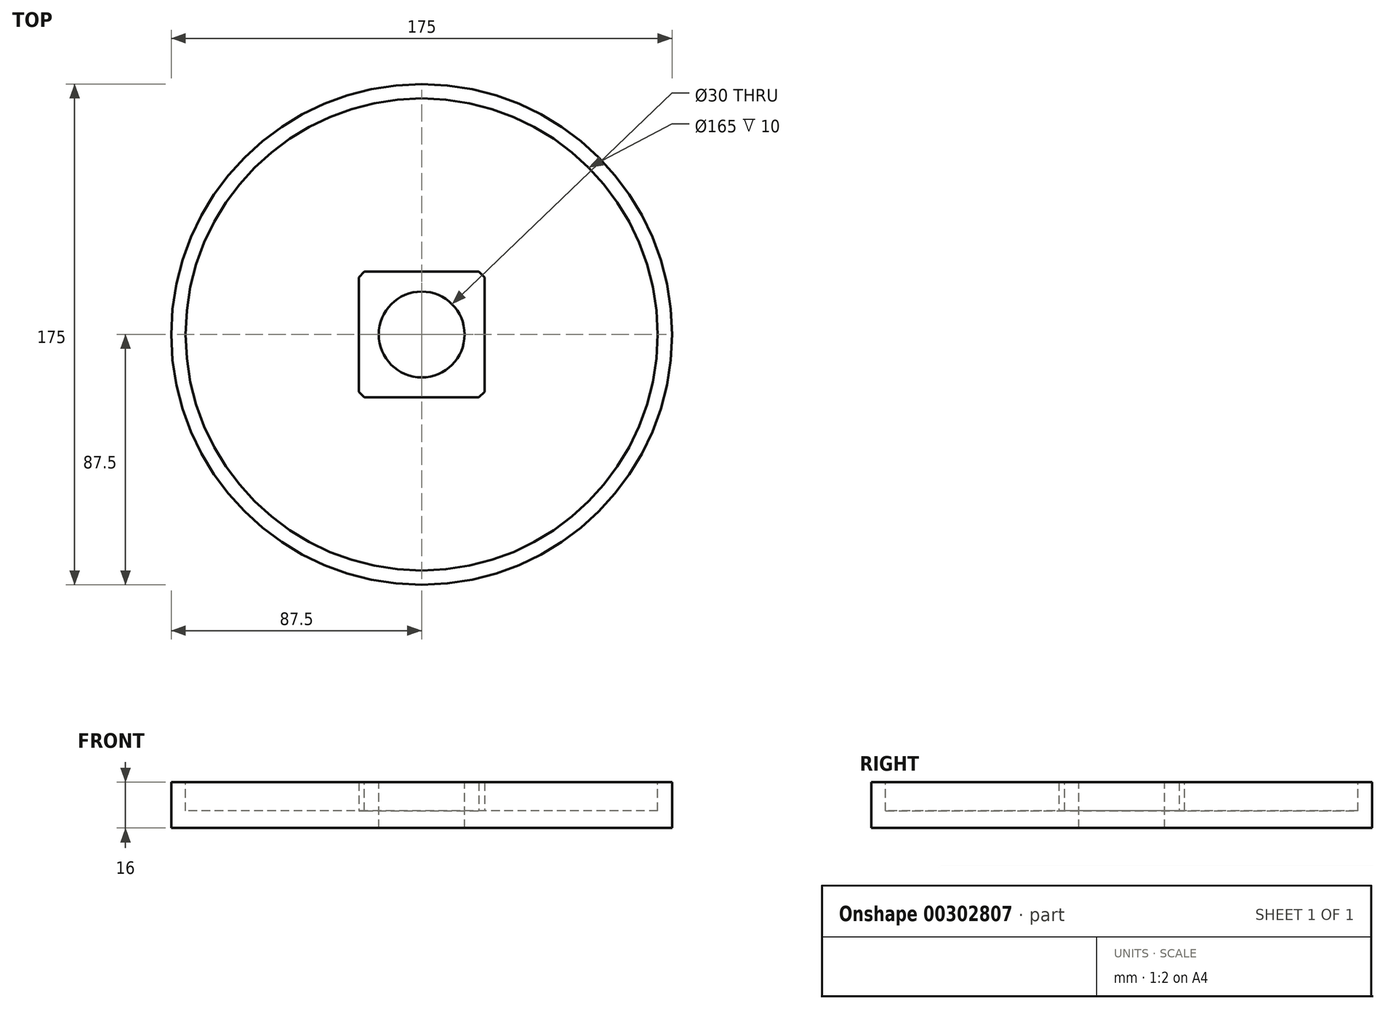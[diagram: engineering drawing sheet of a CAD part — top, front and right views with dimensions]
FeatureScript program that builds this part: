
annotation { "Feature Type Name" : "Feature", "Feature Type Description" : "" }
export const myFeature = defineFeature(function(context is Context, id is Id, definition is map)
    precondition{}
    {
        {
            var Q0;
            Q0=qCreatedBy(makeId("Top.planeOp"),FACE);
            var sketch = newSketch(context, id + "F0", { "sketchPlane" : qUnion([Q0])});
            skCircle(sketch, "E0", {"center": v(0, 0) * mm, "radius": 87.5 * mm});
            skCircle(sketch, "E1", {"center": v(0, 0) * mm, "radius": 82.5 * mm});
            skCircle(sketch, "E2", {"center": v(0, 0) * mm, "radius": 15 * mm});
            skSolve(sketch);
        }
        {
            var Q0;
            Q0=makeQuery(id+"F0.imprint","IMPRINT",FACE,{"disambiguationData":[TD([[makeQuery(id+"F0.imprint","IMPRINT",EDGE,{"derivedFrom":sQuery(id+"F0.wireOp",EDGE,"E0")}),1.0]])]});
            var Q1;
            Q1=makeQuery(id+"F0.imprint","IMPRINT",FACE,{"disambiguationData":[TD([[makeQuery(id+"F0.imprint","IMPRINT",EDGE,{"derivedFrom":sQuery(id+"F0.wireOp",EDGE,"E1")}),1.0]])]});
            extrude(context, id + "F1", {"entities" : qUnion([Q0, Q1]), "oppositeDirection" : true, "depth" : 16 * mm});
        }
        {
            var Q0;
            Q0=makeQuery(id+"F0.imprint","IMPRINT",FACE,{"disambiguationData":[TD([[makeQuery(id+"F0.imprint","IMPRINT",EDGE,{"derivedFrom":sQuery(id+"F0.wireOp",EDGE,"E1")}),1.0]])]});
            extrude(context, id + "F2", {"entities" : qUnion([Q0]), "operationType" : NewBodyOperationType.REMOVE, "oppositeDirection" : true, "depth" : 10 * mm});
        }
        {
            var Q0;
            Q0=makeQuery(id+"F2.boolean.opBoolean","COPY",FACE,{"derivedFrom":makeQuery(id+"F2.opExtrude","CAP_FACE",FACE,{"disambiguationData":[OSD([sQuery(id+"F0.wireOp",EDGE,"E1"),sQuery(id+"F0.wireOp",EDGE,"E2")])],"isStart":false})});
            var sketch = newSketch(context, id + "F3", { "sketchPlane" : qUnion([Q0])});
            skLineSegment(sketch, "E3.bottom", {"start": v(-22, 22) * mm, "end": v(22, 22) * mm});
            skLineSegment(sketch, "E3.top", {"start": v(-22, -22) * mm, "end": v(22, -22) * mm});
            skLineSegment(sketch, "E3.left", {"start": v(-22, 22) * mm, "end": v(-22, -22) * mm});
            skLineSegment(sketch, "E3.right", {"start": v(22, 22) * mm, "end": v(22, -22) * mm});
            skSolve(sketch);
        }
        {
            var Q0;
            Q0=makeQuery(id+"F3.imprint","IMPRINT",FACE,{"disambiguationData":[TD([[makeQuery(id+"F3.imprint","IMPRINT",EDGE,{"derivedFrom":sQuery(id+"F3.wireOp",EDGE,"E3.bottom")}),-1.0]])]});
            extrude(context, id + "F4", {"entities" : qUnion([Q0]), "operationType" : NewBodyOperationType.ADD, "depth" : 10 * mm});
        }
        {
            var Q0;
            Q0=makeQuery(id+"F4.opExtrude","SWEPT_EDGE",EDGE,{"disambiguationData":[OSD([sQuery(id+"F3.wireOp",EDGE,"E3.top"),sQuery(id+"F3.wireOp",EDGE,"E3.right")])]});
            var Q1;
            Q1=makeQuery(id+"F4.opExtrude","SWEPT_EDGE",EDGE,{"disambiguationData":[OSD([sQuery(id+"F3.wireOp",EDGE,"E3.top"),sQuery(id+"F3.wireOp",EDGE,"E3.left")])]});
            var Q2;
            Q2=makeQuery(id+"F4.opExtrude","SWEPT_EDGE",EDGE,{"disambiguationData":[OSD([sQuery(id+"F3.wireOp",EDGE,"E3.bottom"),sQuery(id+"F3.wireOp",EDGE,"E3.right")])]});
            var Q3;
            Q3=makeQuery(id+"F4.opExtrude","SWEPT_EDGE",EDGE,{"disambiguationData":[OSD([sQuery(id+"F3.wireOp",EDGE,"E3.bottom"),sQuery(id+"F3.wireOp",EDGE,"E3.left")])]});
            chamfer(context, id + "F5", {"entities" : qUnion([Q0, Q1, Q2, Q3]), "width" : 2 * mm, "tangentPropagation" : true});
        }
    });
